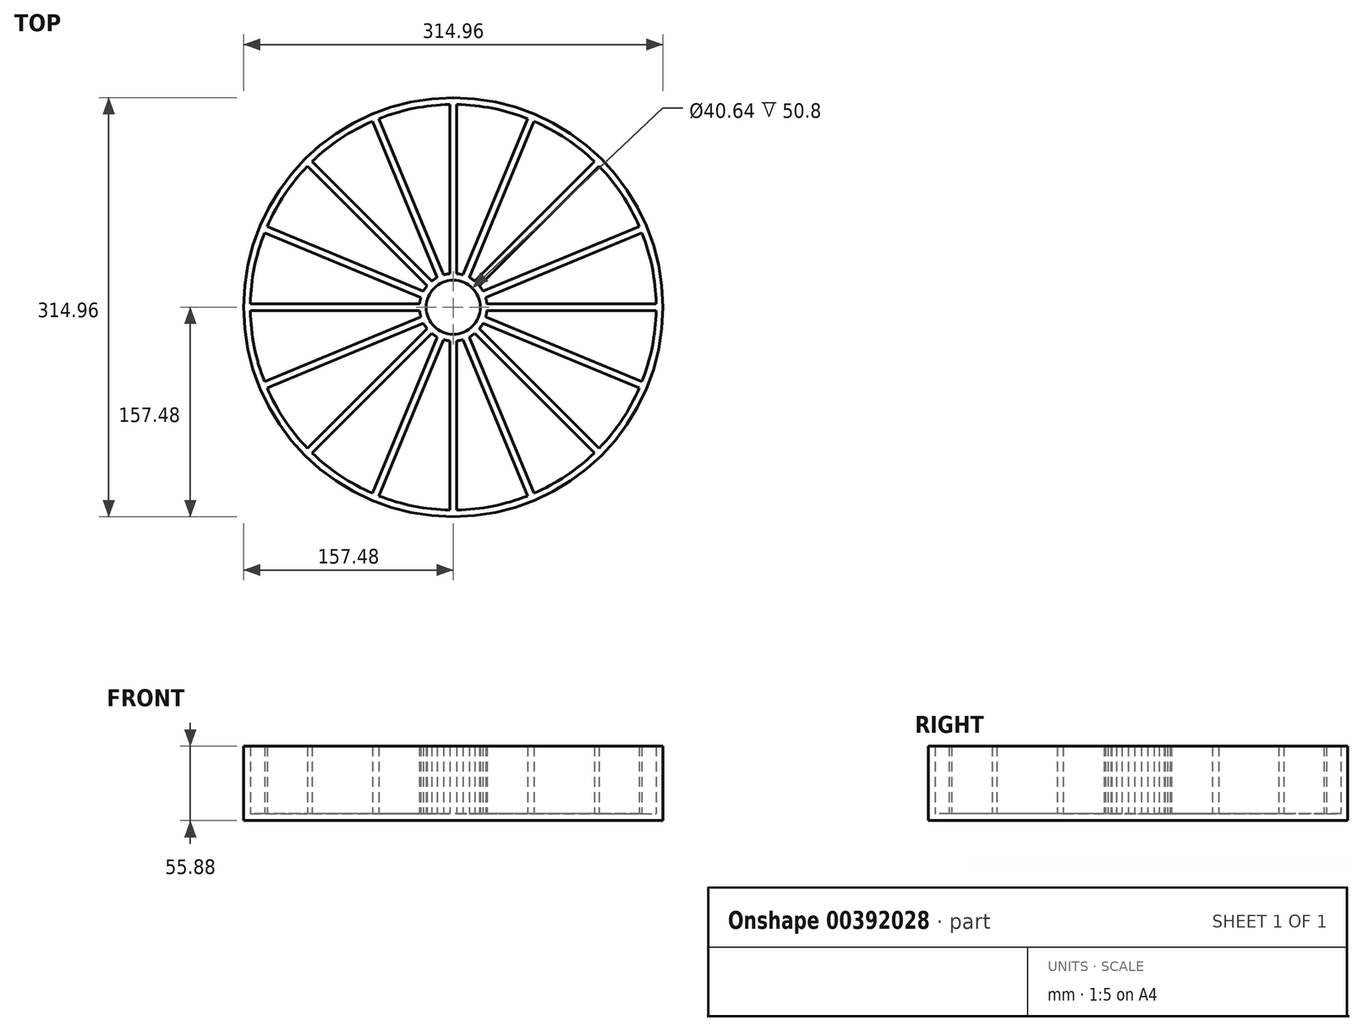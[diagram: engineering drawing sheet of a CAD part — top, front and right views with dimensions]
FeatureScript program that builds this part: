
annotation { "Feature Type Name" : "Feature", "Feature Type Description" : "" }
export const myFeature = defineFeature(function(context is Context, id is Id, definition is map)
    precondition{}
    {
        {
            var Q0;
            Q0=qCreatedBy(makeId("Top.planeOp"),FACE);
            var sketch = newSketch(context, id + "F0", { "sketchPlane" : qUnion([Q0])});
            skCircle(sketch, "E0", {"center": v(0, 0) * mm, "radius": 152.4 * mm});
            skLineSegment(sketch, "E1.0", {"start": v(-2.54, 152.4) * mm, "end": v(-2.54, 25.27) * mm});
            skLineSegment(sketch, "E2.0", {"start": v(2.54, 152.4) * mm, "end": v(2.54, 25.27) * mm});
            skLineSegment(sketch, "E3.0", {"start": v(55.97, 141.77) * mm, "end": v(7.32, 24.32) * mm});
            skLineSegment(sketch, "E4.0", {"start": v(60.67, 139.83) * mm, "end": v(12.02, 22.38) * mm});
            skLineSegment(sketch, "E5.0", {"start": v(105.97, 109.56) * mm, "end": v(16.07, 19.67) * mm});
            skLineSegment(sketch, "E6.0", {"start": v(109.56, 105.97) * mm, "end": v(19.67, 16.07) * mm});
            skLineSegment(sketch, "E7.0", {"start": v(139.83, 60.67) * mm, "end": v(22.38, 12.02) * mm});
            skLineSegment(sketch, "E8.0", {"start": v(141.77, 55.97) * mm, "end": v(24.32, 7.32) * mm});
            skLineSegment(sketch, "E9.0", {"start": v(-152.4, -2.54) * mm, "end": v(-25.27, -2.54) * mm});
            skLineSegment(sketch, "E10.0", {"start": v(-152.4, 2.54) * mm, "end": v(-25.27, 2.54) * mm});
            skLineSegment(sketch, "E11.0", {"start": v(141.77, -55.97) * mm, "end": v(24.32, -7.32) * mm});
            skLineSegment(sketch, "E12.0", {"start": v(139.83, -60.67) * mm, "end": v(22.38, -12.02) * mm});
            skLineSegment(sketch, "E13.0", {"start": v(109.56, -105.97) * mm, "end": v(19.67, -16.07) * mm});
            skLineSegment(sketch, "E14.0", {"start": v(105.97, -109.56) * mm, "end": v(16.07, -19.67) * mm});
            skLineSegment(sketch, "E15.0", {"start": v(-60.67, 139.83) * mm, "end": v(-12.02, 22.38) * mm});
            skLineSegment(sketch, "E16.0", {"start": v(-55.97, 141.77) * mm, "end": v(-7.32, 24.32) * mm});
            skCircle(sketch, "E17.0", {"center": v(0, 0) * mm, "radius": 157.48 * mm});
            skCircle(sketch, "E18", {"center": v(0, 0) * mm, "radius": 25.4 * mm});
            skLineSegment(sketch, "E19.trimOffspring", {"start": v(-16.07, 19.67) * mm, "end": v(-105.97, 109.56) * mm});
            skLineSegment(sketch, "E20.trimOffspring", {"start": v(-19.67, 16.07) * mm, "end": v(-109.56, 105.97) * mm});
            skLineSegment(sketch, "E21.trimOffspring", {"start": v(-22.38, 12.02) * mm, "end": v(-139.83, 60.67) * mm});
            skLineSegment(sketch, "E22.trimOffspring", {"start": v(12.02, -22.38) * mm, "end": v(60.67, -139.83) * mm});
            skLineSegment(sketch, "E23.trimOffspring", {"start": v(-24.32, 7.32) * mm, "end": v(-141.77, 55.97) * mm});
            skLineSegment(sketch, "E24.trimOffspring", {"start": v(-24.32, -7.32) * mm, "end": v(-141.77, -55.97) * mm});
            skLineSegment(sketch, "E25.trimOffspring", {"start": v(-19.67, -16.07) * mm, "end": v(-109.56, -105.97) * mm});
            skLineSegment(sketch, "E26.trimOffspring", {"start": v(25.27, -2.54) * mm, "end": v(152.4, -2.54) * mm});
            skLineSegment(sketch, "E27.trimOffspring", {"start": v(25.27, 2.54) * mm, "end": v(152.4, 2.54) * mm});
            skLineSegment(sketch, "E28.trimOffspring", {"start": v(-22.38, -12.02) * mm, "end": v(-139.83, -60.67) * mm});
            skLineSegment(sketch, "E29.trimOffspring", {"start": v(-16.07, -19.67) * mm, "end": v(-105.97, -109.56) * mm});
            skLineSegment(sketch, "E30.trimOffspring", {"start": v(-12.02, -22.38) * mm, "end": v(-60.67, -139.83) * mm});
            skLineSegment(sketch, "E31.trimOffspring", {"start": v(-7.32, -24.32) * mm, "end": v(-55.97, -141.77) * mm});
            skLineSegment(sketch, "E32.trimOffspring", {"start": v(-2.54, -25.27) * mm, "end": v(-2.54, -152.4) * mm});
            skLineSegment(sketch, "E33.trimOffspring", {"start": v(7.32, -24.32) * mm, "end": v(55.97, -141.77) * mm});
            skLineSegment(sketch, "E34.trimOffspring", {"start": v(2.54, -25.27) * mm, "end": v(2.54, -152.4) * mm});
            skCircle(sketch, "E35.0", {"center": v(0, 0) * mm, "radius": 20.32 * mm});
            skSolve(sketch);
        }
        {
            var Q0;
            Q0 = qSketchRegion(id + "F0", true);
            var Q1;
            {var subQ0=sQuery(id+"F0.wireOp",EDGE,"E16.0");var subQ1=sQuery(id+"F0.wireOp",EDGE,"E0");var subQ2=makeQuery(id+"F0.imprint","INTERSECT",VERTEX,{"derivedFrom":[subQ1,subQ0]});Q1=makeQuery(id+"F0.imprint","IMPRINT",FACE,{"disambiguationData":[TD([[makeQuery(id+"F0.imprint","IMPRINT",EDGE,{"disambiguationData":[TD([[subQ2,-1.0]])],"derivedFrom":subQ1}),1.0]])]});}
            var Q2;
            {var subQ0=sQuery(id+"F0.wireOp",EDGE,"E19.trimOffspring");var subQ1=sQuery(id+"F0.wireOp",EDGE,"E0");var subQ2=makeQuery(id+"F0.imprint","INTERSECT",VERTEX,{"derivedFrom":[subQ1,subQ0]});Q2=makeQuery(id+"F0.imprint","IMPRINT",FACE,{"disambiguationData":[TD([[makeQuery(id+"F0.imprint","IMPRINT",EDGE,{"disambiguationData":[TD([[subQ2,-1.0]])],"derivedFrom":subQ1}),1.0]])]});}
            var Q3;
            {var subQ0=sQuery(id+"F0.wireOp",EDGE,"E21.trimOffspring");var subQ1=sQuery(id+"F0.wireOp",EDGE,"E0");var subQ2=makeQuery(id+"F0.imprint","INTERSECT",VERTEX,{"derivedFrom":[subQ1,subQ0]});Q3=makeQuery(id+"F0.imprint","IMPRINT",FACE,{"disambiguationData":[TD([[makeQuery(id+"F0.imprint","IMPRINT",EDGE,{"disambiguationData":[TD([[subQ2,-1.0]])],"derivedFrom":subQ1}),1.0]])]});}
            var Q4;
            {var subQ0=sQuery(id+"F0.wireOp",EDGE,"E10.0");var subQ1=sQuery(id+"F0.wireOp",EDGE,"E0");var subQ2=makeQuery(id+"F0.imprint","INTERSECT",VERTEX,{"derivedFrom":[subQ1,subQ0]});Q4=makeQuery(id+"F0.imprint","IMPRINT",FACE,{"disambiguationData":[TD([[makeQuery(id+"F0.imprint","IMPRINT",EDGE,{"disambiguationData":[TD([[subQ2,-1.0]])],"derivedFrom":subQ1}),1.0]])]});}
            var Q5;
            {var subQ0=sQuery(id+"F0.wireOp",EDGE,"E24.trimOffspring");var subQ1=sQuery(id+"F0.wireOp",EDGE,"E0");var subQ2=makeQuery(id+"F0.imprint","INTERSECT",VERTEX,{"derivedFrom":[subQ1,subQ0]});Q5=makeQuery(id+"F0.imprint","IMPRINT",FACE,{"disambiguationData":[TD([[makeQuery(id+"F0.imprint","IMPRINT",EDGE,{"disambiguationData":[TD([[subQ2,-1.0]])],"derivedFrom":subQ1}),1.0]])]});}
            var Q6;
            {var subQ0=sQuery(id+"F0.wireOp",EDGE,"E25.trimOffspring");var subQ1=sQuery(id+"F0.wireOp",EDGE,"E0");var subQ2=makeQuery(id+"F0.imprint","INTERSECT",VERTEX,{"derivedFrom":[subQ1,subQ0]});Q6=makeQuery(id+"F0.imprint","IMPRINT",FACE,{"disambiguationData":[TD([[makeQuery(id+"F0.imprint","IMPRINT",EDGE,{"disambiguationData":[TD([[subQ2,-1.0]])],"derivedFrom":subQ1}),1.0]])]});}
            var Q7;
            {var subQ0=sQuery(id+"F0.wireOp",EDGE,"E30.trimOffspring");var subQ1=sQuery(id+"F0.wireOp",EDGE,"E0");var subQ2=makeQuery(id+"F0.imprint","INTERSECT",VERTEX,{"derivedFrom":[subQ1,subQ0]});Q7=makeQuery(id+"F0.imprint","IMPRINT",FACE,{"disambiguationData":[TD([[makeQuery(id+"F0.imprint","IMPRINT",EDGE,{"disambiguationData":[TD([[subQ2,-1.0]])],"derivedFrom":subQ1}),1.0]])]});}
            var Q8;
            {var subQ0=sQuery(id+"F0.wireOp",EDGE,"E32.trimOffspring");var subQ1=sQuery(id+"F0.wireOp",EDGE,"E0");var subQ2=makeQuery(id+"F0.imprint","INTERSECT",VERTEX,{"derivedFrom":[subQ1,subQ0]});Q8=makeQuery(id+"F0.imprint","IMPRINT",FACE,{"disambiguationData":[TD([[makeQuery(id+"F0.imprint","IMPRINT",EDGE,{"disambiguationData":[TD([[subQ2,-1.0]])],"derivedFrom":subQ1}),1.0]])]});}
            var Q9;
            {var subQ0=sQuery(id+"F0.wireOp",EDGE,"E33.trimOffspring");var subQ1=sQuery(id+"F0.wireOp",EDGE,"E0");var subQ2=makeQuery(id+"F0.imprint","INTERSECT",VERTEX,{"derivedFrom":[subQ1,subQ0]});Q9=makeQuery(id+"F0.imprint","IMPRINT",FACE,{"disambiguationData":[TD([[makeQuery(id+"F0.imprint","IMPRINT",EDGE,{"disambiguationData":[TD([[subQ2,-1.0]])],"derivedFrom":subQ1}),1.0]])]});}
            var Q10;
            {var subQ0=sQuery(id+"F0.wireOp",EDGE,"E14.0");var subQ1=sQuery(id+"F0.wireOp",EDGE,"E0");var subQ2=makeQuery(id+"F0.imprint","INTERSECT",VERTEX,{"derivedFrom":[subQ1,subQ0]});Q10=makeQuery(id+"F0.imprint","IMPRINT",FACE,{"disambiguationData":[TD([[makeQuery(id+"F0.imprint","IMPRINT",EDGE,{"disambiguationData":[TD([[subQ2,-1.0]])],"derivedFrom":subQ1}),1.0]])]});}
            var Q11;
            {var subQ0=sQuery(id+"F0.wireOp",EDGE,"E12.0");var subQ1=sQuery(id+"F0.wireOp",EDGE,"E0");var subQ2=makeQuery(id+"F0.imprint","INTERSECT",VERTEX,{"derivedFrom":[subQ1,subQ0]});Q11=makeQuery(id+"F0.imprint","IMPRINT",FACE,{"disambiguationData":[TD([[makeQuery(id+"F0.imprint","IMPRINT",EDGE,{"disambiguationData":[TD([[subQ2,-1.0]])],"derivedFrom":subQ1}),1.0]])]});}
            var Q12;
            {var subQ0=sQuery(id+"F0.wireOp",EDGE,"E27.trimOffspring");var subQ1=sQuery(id+"F0.wireOp",EDGE,"E0");var subQ2=makeQuery(id+"F0.imprint","INTERSECT",VERTEX,{"derivedFrom":[subQ1,subQ0]});Q12=makeQuery(id+"F0.imprint","IMPRINT",FACE,{"disambiguationData":[TD([[makeQuery(id+"F0.imprint","IMPRINT",EDGE,{"disambiguationData":[TD([[subQ2,1.0]])],"derivedFrom":subQ1}),1.0]])]});}
            var Q13;
            {var subQ0=sQuery(id+"F0.wireOp",EDGE,"E8.0");var subQ1=sQuery(id+"F0.wireOp",EDGE,"E0");var subQ2=makeQuery(id+"F0.imprint","INTERSECT",VERTEX,{"derivedFrom":[subQ1,subQ0]});Q13=makeQuery(id+"F0.imprint","IMPRINT",FACE,{"disambiguationData":[TD([[makeQuery(id+"F0.imprint","IMPRINT",EDGE,{"disambiguationData":[TD([[subQ2,-1.0]])],"derivedFrom":subQ1}),1.0]])]});}
            var Q14;
            {var subQ0=sQuery(id+"F0.wireOp",EDGE,"E6.0");var subQ1=sQuery(id+"F0.wireOp",EDGE,"E0");var subQ2=makeQuery(id+"F0.imprint","INTERSECT",VERTEX,{"derivedFrom":[subQ1,subQ0]});Q14=makeQuery(id+"F0.imprint","IMPRINT",FACE,{"disambiguationData":[TD([[makeQuery(id+"F0.imprint","IMPRINT",EDGE,{"disambiguationData":[TD([[subQ2,-1.0]])],"derivedFrom":subQ1}),1.0]])]});}
            var Q15;
            {var subQ0=sQuery(id+"F0.wireOp",EDGE,"E4.0");var subQ1=sQuery(id+"F0.wireOp",EDGE,"E0");var subQ2=makeQuery(id+"F0.imprint","INTERSECT",VERTEX,{"derivedFrom":[subQ1,subQ0]});Q15=makeQuery(id+"F0.imprint","IMPRINT",FACE,{"disambiguationData":[TD([[makeQuery(id+"F0.imprint","IMPRINT",EDGE,{"disambiguationData":[TD([[subQ2,-1.0]])],"derivedFrom":subQ1}),1.0]])]});}
            var Q16;
            {var subQ0=sQuery(id+"F0.wireOp",EDGE,"E2.0");var subQ1=sQuery(id+"F0.wireOp",EDGE,"E0");var subQ2=makeQuery(id+"F0.imprint","INTERSECT",VERTEX,{"derivedFrom":[subQ1,subQ0]});Q16=makeQuery(id+"F0.imprint","IMPRINT",FACE,{"disambiguationData":[TD([[makeQuery(id+"F0.imprint","IMPRINT",EDGE,{"disambiguationData":[TD([[subQ2,-1.0]])],"derivedFrom":subQ1}),1.0]])]});}
            var Q17;
            Q17=makeQuery(id+"F0.imprint","IMPRINT",FACE,{"disambiguationData":[TD([[makeQuery(id+"F0.imprint","IMPRINT",EDGE,{"derivedFrom":sQuery(id+"F0.wireOp",EDGE,"E35.0")}),-1.0]])]});
            extrude(context, id + "F1", {"entities" : qUnion([Q0, Q1, Q2, Q3, Q4, Q5, Q6, Q7, Q8, Q9, Q10, Q11, Q12, Q13, Q14, Q15, Q16, Q17]), "depth" : 50.8 * mm});
        }
        {
            var Q0;
            Q0=makeQuery(id+"F1.opExtrude","CAP_FACE",FACE,{"disambiguationData":[OSD([sQuery(id+"F0.wireOp",EDGE,"E0"),sQuery(id+"F0.wireOp",EDGE,"E1.0"),sQuery(id+"F0.wireOp",EDGE,"E2.0"),sQuery(id+"F0.wireOp",EDGE,"E3.0"),sQuery(id+"F0.wireOp",EDGE,"E4.0"),sQuery(id+"F0.wireOp",EDGE,"E5.0"),sQuery(id+"F0.wireOp",EDGE,"E6.0"),sQuery(id+"F0.wireOp",EDGE,"E7.0"),sQuery(id+"F0.wireOp",EDGE,"E8.0"),sQuery(id+"F0.wireOp",EDGE,"E9.0"),sQuery(id+"F0.wireOp",EDGE,"E10.0"),sQuery(id+"F0.wireOp",EDGE,"E11.0"),sQuery(id+"F0.wireOp",EDGE,"E12.0"),sQuery(id+"F0.wireOp",EDGE,"E13.0"),sQuery(id+"F0.wireOp",EDGE,"E14.0"),sQuery(id+"F0.wireOp",EDGE,"E15.0"),sQuery(id+"F0.wireOp",EDGE,"E16.0"),sQuery(id+"F0.wireOp",EDGE,"E17.0"),sQuery(id+"F0.wireOp",EDGE,"E18"),sQuery(id+"F0.wireOp",EDGE,"E19.trimOffspring"),sQuery(id+"F0.wireOp",EDGE,"E20.trimOffspring"),sQuery(id+"F0.wireOp",EDGE,"E21.trimOffspring"),sQuery(id+"F0.wireOp",EDGE,"E22.trimOffspring"),sQuery(id+"F0.wireOp",EDGE,"E23.trimOffspring"),sQuery(id+"F0.wireOp",EDGE,"E24.trimOffspring"),sQuery(id+"F0.wireOp",EDGE,"E25.trimOffspring"),sQuery(id+"F0.wireOp",EDGE,"E26.trimOffspring"),sQuery(id+"F0.wireOp",EDGE,"E27.trimOffspring"),sQuery(id+"F0.wireOp",EDGE,"E28.trimOffspring"),sQuery(id+"F0.wireOp",EDGE,"E29.trimOffspring"),sQuery(id+"F0.wireOp",EDGE,"E30.trimOffspring"),sQuery(id+"F0.wireOp",EDGE,"E31.trimOffspring"),sQuery(id+"F0.wireOp",EDGE,"E32.trimOffspring"),sQuery(id+"F0.wireOp",EDGE,"E33.trimOffspring"),sQuery(id+"F0.wireOp",EDGE,"E34.trimOffspring"),sQuery(id+"F0.wireOp",EDGE,"E35.0")])],"isStart":true});
            var sketch = newSketch(context, id + "F2", { "sketchPlane" : qUnion([Q0])});
            skCircle(sketch, "E36", {"center": v(0, 0) * mm, "radius": 157.48 * mm});
            skSolve(sketch);
        }
        {
            var Q0;
            Q0 = qSketchRegion(id + "F2", true);
            extrude(context, id + "F3", {"entities" : qUnion([Q0]), "operationType" : NewBodyOperationType.ADD, "depth" : 5.08 * mm});
        }
    });
